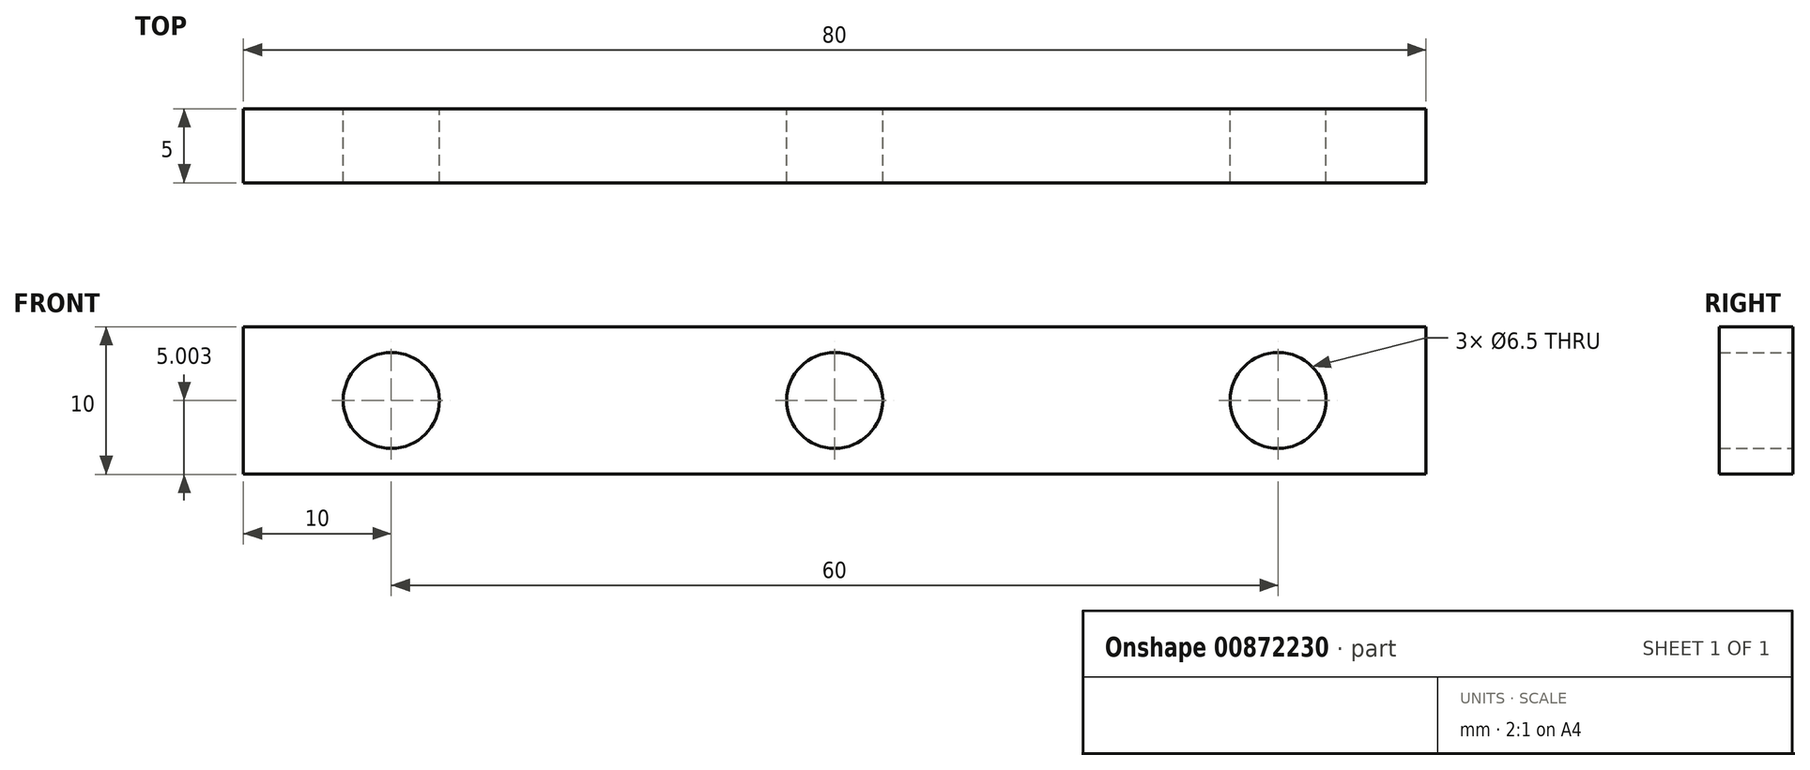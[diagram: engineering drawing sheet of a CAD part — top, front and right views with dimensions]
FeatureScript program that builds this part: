
annotation { "Feature Type Name" : "Feature", "Feature Type Description" : "" }
export const myFeature = defineFeature(function(context is Context, id is Id, definition is map)
    precondition{}
    {
        {
            var Q0;
            Q0=qCreatedBy(makeId("Front.planeOp"),FACE);
            var sketch = newSketch(context, id + "F0", { "sketchPlane" : qUnion([Q0])});
            skLineSegment(sketch, "E0.bottom", {"start": v(-40, -1.1) * mm, "end": v(40, -1.1) * mm});
            skLineSegment(sketch, "E0.top", {"start": v(-40, -11.1) * mm, "end": v(40, -11.1) * mm});
            skLineSegment(sketch, "E0.left", {"start": v(-40, -1.1) * mm, "end": v(-40, -11.1) * mm});
            skLineSegment(sketch, "E1", {"start": v(40, -1.1) * mm, "end": v(40, -11.1) * mm});
            skPoint(sketch, "E2", {"position": v(-55, -11.1) * mm});
            skPoint(sketch, "E3", {"position": v(-30, -6.1) * mm});
            skPoint(sketch, "E3.positionSnap0", {"position": v(-40, -6.1) * mm});
            skPoint(sketch, "E4", {"position": v(30, -6.1) * mm});
            skPoint(sketch, "E4.positionSnap0", {"position": v(40, -6.1) * mm});
            skPoint(sketch, "E5", {"position": v(0, -6.1) * mm});
            skCircle(sketch, "E6", {"center": v(-30, -6.1) * mm, "radius": 3.25 * mm});
            skCircle(sketch, "E7", {"center": v(0, -6.1) * mm, "radius": 3.25 * mm});
            skCircle(sketch, "E8", {"center": v(30, -6.1) * mm, "radius": 3.25 * mm});
            skSolve(sketch);
        }
        {
            var Q0;
            Q0=qSketchRegion(id+"F0",true);
            extrude(context, id + "F1", {"entities" : qUnion([Q0]), "depth" : 5 * mm, "offsetDistance" : 25 * mm});
        }
        {
            var Q0;
            Q0=qSketchRegion(id+"F0",true);
            extrude(context, id + "F2", {"entities" : qUnion([Q0]), "operationType" : NewBodyOperationType.ADD, "depth" : 5 * mm, "offsetDistance" : 25 * mm});
        }
    });
